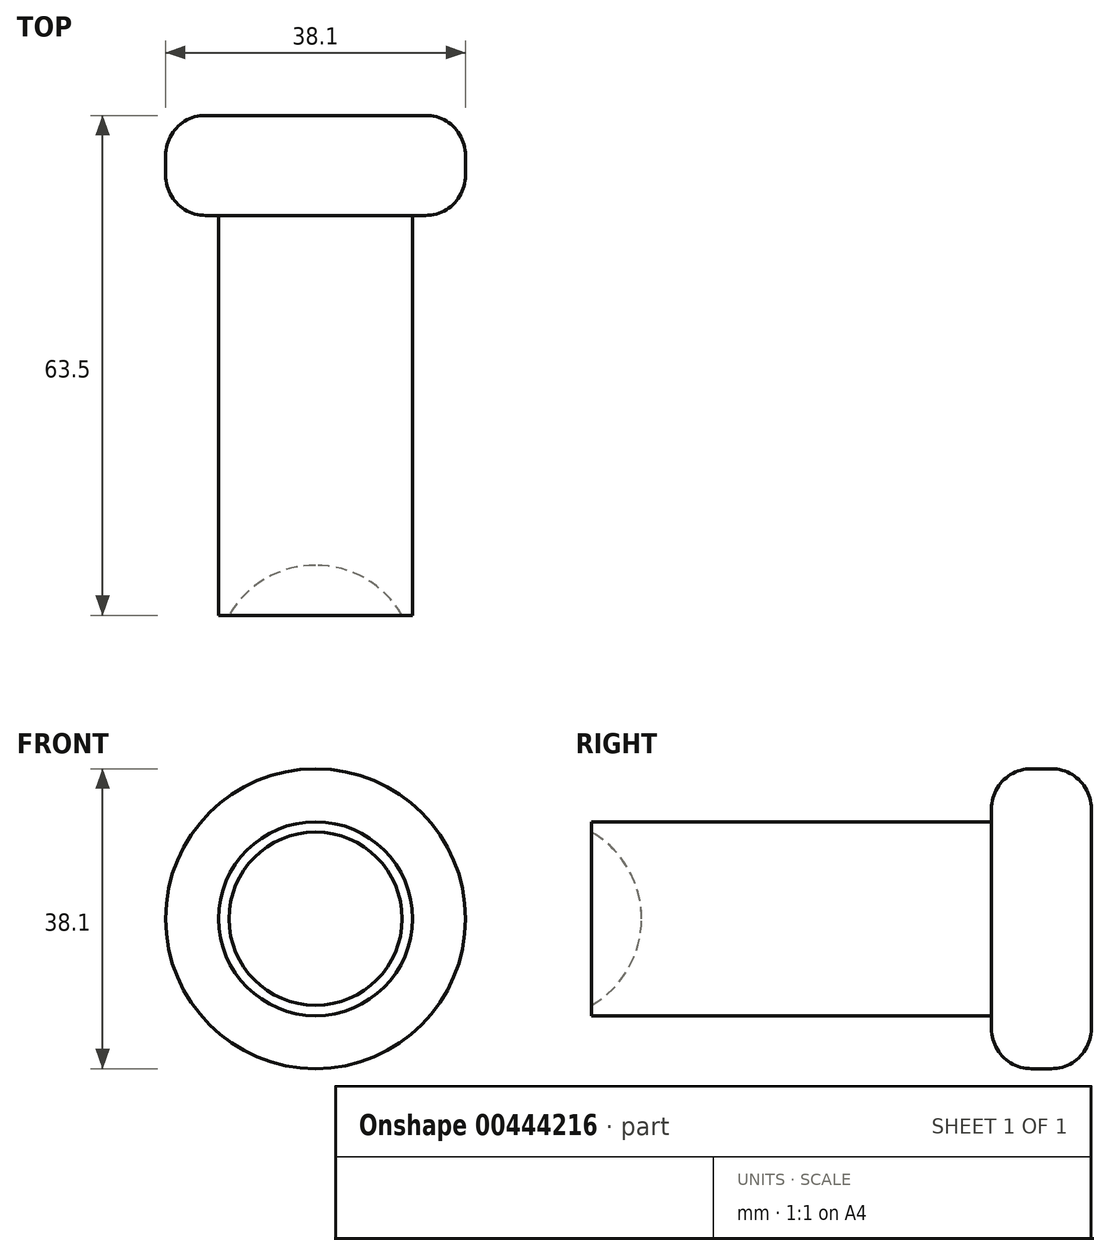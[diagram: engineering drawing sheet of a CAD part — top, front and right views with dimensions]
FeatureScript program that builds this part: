
annotation { "Feature Type Name" : "Feature", "Feature Type Description" : "" }
export const myFeature = defineFeature(function(context is Context, id is Id, definition is map)
    precondition{}
    {
        {
            var Q0;
            Q0=qCreatedBy(makeId("Right.planeOp"),FACE);
            var sketch = newSketch(context, id + "F0", { "sketchPlane" : qUnion([Q0])});
            skLineSegment(sketch, "E0", {"start": v(-67.4, 0) * mm, "end": v(67.5, 0) * mm});
            skLineSegment(sketch, "E1.bottom", {"start": v(-50.8, 0) * mm, "end": v(21.23, 0) * mm});
            skLineSegment(sketch, "E1.top", {"start": v(-50.8, 12.32) * mm, "end": v(0, 12.32) * mm});
            skLineSegment(sketch, "E1.left", {"start": v(-50.8, 11) * mm, "end": v(-50.8, 12.32) * mm});
            skLineSegment(sketch, "E2.bottom", {"start": v(12.7, 0) * mm, "end": v(21.23, 0) * mm});
            skLineSegment(sketch, "E2.top", {"start": v(0, 19.05) * mm, "end": v(12.7, 19.05) * mm});
            skLineSegment(sketch, "E2.right", {"start": v(12.7, 0) * mm, "end": v(12.7, 19.05) * mm});
            skLineSegment(sketch, "E3", {"start": v(0, 19.05) * mm, "end": v(0, 12.32) * mm});
            skArc(sketch, "E4", {"start": v(-44.45, 0) * mm, "mid": v(-46.15, 6.35) * mm, "end": v(-50.8, 11) * mm});
            skSolve(sketch);
        }
        {
            var Q0;
            Q0 = qSketchRegion(id + "F0", true);
            var Q1;
            Q1=sQuery(id+"F0.wireOp",EDGE,"E0");
            revolve(context, id + "F1", {"entities" : qUnion([Q0]), "axis" : qUnion([Q1]), "revolveType" : RevolveType.FULL});
        }
        {
            var Q0;
            Q0=makeQuery(id+"F1.opRevolve","SWEPT_EDGE",EDGE,{"disambiguationData":[OSD([sQuery(id+"F0.wireOp",EDGE,"E2.top"),sQuery(id+"F0.wireOp",EDGE,"E2.right")])]});
            var Q1;
            Q1=makeQuery(id+"F1.opRevolve","SWEPT_EDGE",EDGE,{"disambiguationData":[OSD([sQuery(id+"F0.wireOp",EDGE,"E2.top"),sQuery(id+"F0.wireOp",EDGE,"E3")])]});
            fillet(context, id + "F2", {"entities" : qUnion([Q0, Q1]), "radius" : 5.08 * mm, "tangentPropagation" : true, "allowEdgeOverflow" : false});
        }
    });
